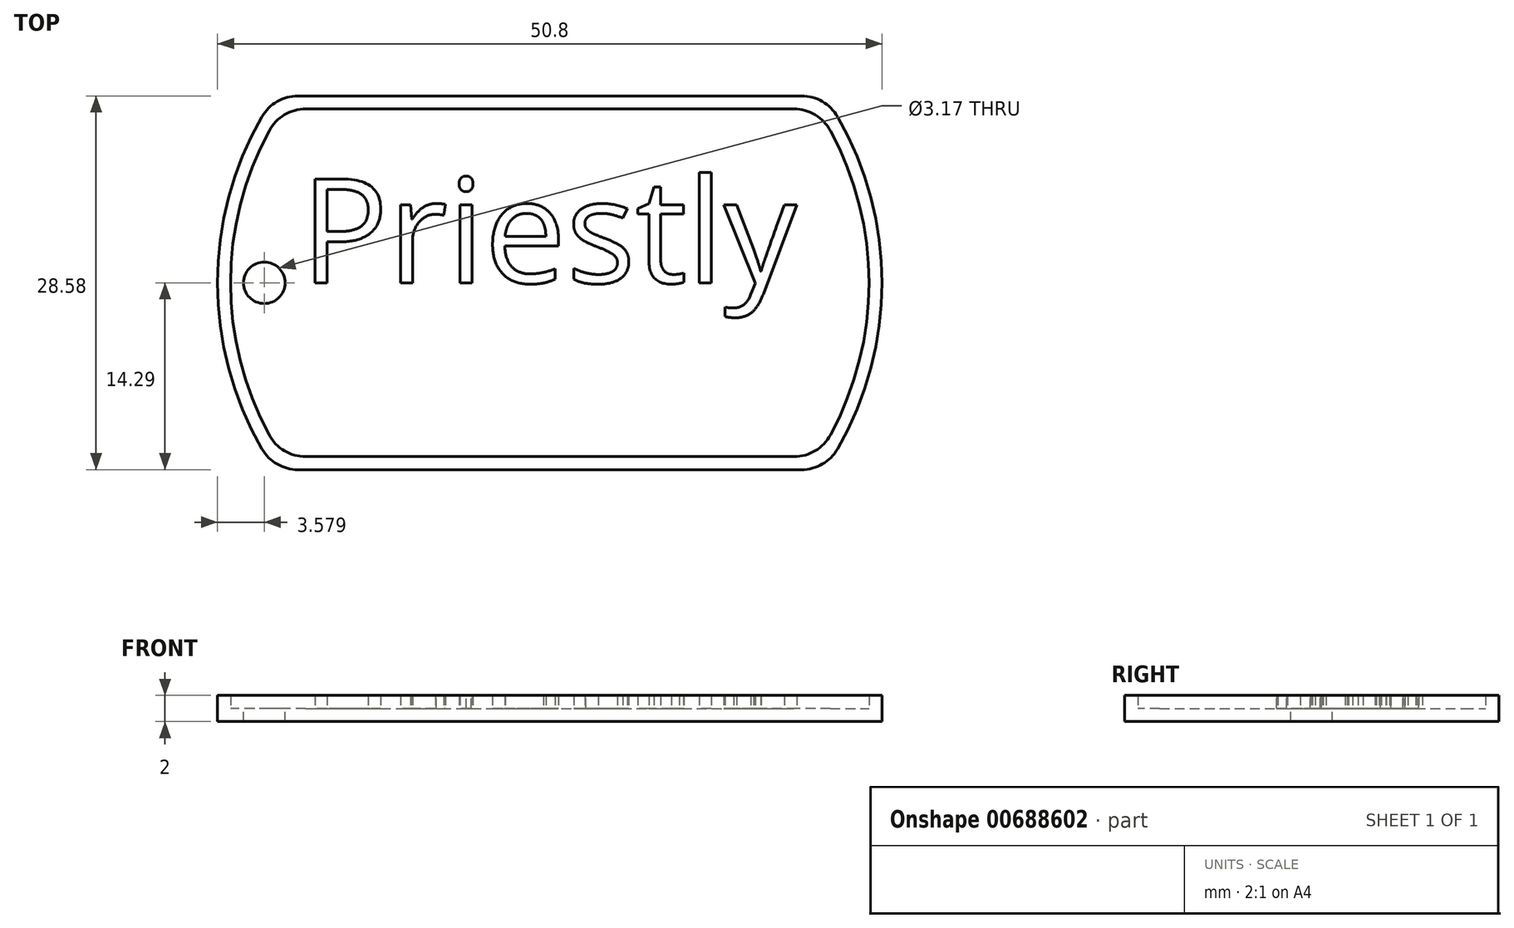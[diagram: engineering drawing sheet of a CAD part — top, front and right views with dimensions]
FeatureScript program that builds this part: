
annotation { "Feature Type Name" : "Feature", "Feature Type Description" : "" }
export const myFeature = defineFeature(function(context is Context, id is Id, definition is map)
    precondition{}
    {
        {
            var Q0;
            Q0=qCreatedBy(makeId("Top.planeOp"),FACE);
            var sketch = newSketch(context, id + "F0", { "sketchPlane" : qUnion([Q0])});
            skArc(sketch, "E0", {"start": v(-22, 12.7) * mm, "mid": v(-25.4, 0) * mm, "end": v(-22, -12.7) * mm});
            skLineSegment(sketch, "E1.top", {"start": v(-19.25, -14.29) * mm, "end": v(19.25, -14.29) * mm});
            skArc(sketch, "E2.trimOffspring", {"start": v(22, -12.7) * mm, "mid": v(25.4, 0) * mm, "end": v(22, 12.7) * mm});
            skLineSegment(sketch, "E3", {"start": v(-19.25, 14.29) * mm, "end": v(19.25, 14.29) * mm});
            skPoint(sketch, "E4.visualSharp", {"position": v(-21, 14.29) * mm});
            skArc(sketch, "E4.filletArc", {"start": v(-19.25, 14.29) * mm, "mid": v(-20.83, 13.86) * mm, "end": v(-22, 12.7) * mm});
            skPoint(sketch, "E5.visualSharp", {"position": v(21, 14.29) * mm});
            skArc(sketch, "E5.filletArc", {"start": v(22, 12.7) * mm, "mid": v(20.83, 13.86) * mm, "end": v(19.25, 14.29) * mm});
            skPoint(sketch, "E6.visualSharp", {"position": v(21, -14.29) * mm});
            skArc(sketch, "E6.filletArc", {"start": v(19.25, -14.29) * mm, "mid": v(20.83, -13.86) * mm, "end": v(22, -12.7) * mm});
            skPoint(sketch, "E7.visualSharp", {"position": v(-21, -14.29) * mm});
            skArc(sketch, "E7.filletArc", {"start": v(-22, -12.7) * mm, "mid": v(-20.83, -13.86) * mm, "end": v(-19.25, -14.29) * mm});
            skSolve(sketch);
        }
        {
            var Q0;
            Q0=makeQuery(id+"F0.imprint","IMPRINT",FACE,{"disambiguationData":[TD([[makeQuery(id+"F0.imprint","IMPRINT",EDGE,{"derivedFrom":sQuery(id+"F0.wireOp",EDGE,"E0")}),1.0]])]});
            extrude(context, id + "F1", {"entities" : qUnion([Q0]), "depth" : 1 * mm, "offsetDistance" : 25.4 * mm});
        }
        {
            var Q0;
            Q0=makeQuery(id+"F1.opExtrude","CAP_FACE",FACE,{"disambiguationData":[OSD([sQuery(id+"F0.wireOp",EDGE,"E0"),sQuery(id+"F0.wireOp",EDGE,"E1.top"),sQuery(id+"F0.wireOp",EDGE,"E2.trimOffspring"),sQuery(id+"F0.wireOp",EDGE,"E3"),sQuery(id+"F0.wireOp",EDGE,"E4.filletArc"),sQuery(id+"F0.wireOp",EDGE,"E5.filletArc"),sQuery(id+"F0.wireOp",EDGE,"E6.filletArc"),sQuery(id+"F0.wireOp",EDGE,"E7.filletArc")])],"isStart":false});
            var sketch = newSketch(context, id + "F2", { "sketchPlane" : qUnion([Q0])});
            skLineSegment(sketch, "E8.0", {"start": v(-18.66, 13.29) * mm, "end": v(18.66, 13.29) * mm});
            skArc(sketch, "E8.1", {"start": v(-21.45, 11.63) * mm, "mid": v(-24.4, 0) * mm, "end": v(-21.45, -11.63) * mm});
            skLineSegment(sketch, "E8.2", {"start": v(-18.66, -13.29) * mm, "end": v(18.66, -13.29) * mm});
            skArc(sketch, "E8.3", {"start": v(21.45, -11.63) * mm, "mid": v(24.4, 0) * mm, "end": v(21.45, 11.63) * mm});
            skPoint(sketch, "E9.visualSharp", {"position": v(-20.46, 13.29) * mm});
            skArc(sketch, "E9.filletArc", {"start": v(-18.66, 13.29) * mm, "mid": v(-20.29, 12.84) * mm, "end": v(-21.45, 11.63) * mm});
            skPoint(sketch, "E10.visualSharp", {"position": v(20.46, 13.29) * mm});
            skArc(sketch, "E10.filletArc", {"start": v(21.45, 11.63) * mm, "mid": v(20.29, 12.84) * mm, "end": v(18.66, 13.29) * mm});
            skPoint(sketch, "E11.visualSharp", {"position": v(20.46, -13.29) * mm});
            skArc(sketch, "E11.filletArc", {"start": v(18.66, -13.29) * mm, "mid": v(20.29, -12.84) * mm, "end": v(21.45, -11.63) * mm});
            skPoint(sketch, "E12.visualSharp", {"position": v(-20.46, -13.29) * mm});
            skArc(sketch, "E12.filletArc", {"start": v(-21.45, -11.63) * mm, "mid": v(-20.29, -12.84) * mm, "end": v(-18.66, -13.29) * mm});
            skLineSegment(sketch, "E13.0", {"start": v(-19.25, 14.29) * mm, "end": v(19.25, 14.29) * mm});
            skArc(sketch, "E13.1", {"start": v(-22, 12.7) * mm, "mid": v(-25.4, 0) * mm, "end": v(-22, -12.7) * mm});
            skLineSegment(sketch, "E13.2", {"start": v(-19.25, -14.29) * mm, "end": v(19.25, -14.29) * mm});
            skArc(sketch, "E13.3", {"start": v(22, -12.7) * mm, "mid": v(25.4, 0) * mm, "end": v(22, 12.7) * mm});
            skPoint(sketch, "E14.visualSharp", {"position": v(-21, -14.29) * mm});
            skArc(sketch, "E14.filletArc", {"start": v(-22, -12.7) * mm, "mid": v(-20.83, -13.86) * mm, "end": v(-19.25, -14.29) * mm});
            skPoint(sketch, "E15.visualSharp", {"position": v(21, -14.29) * mm});
            skArc(sketch, "E15.filletArc", {"start": v(19.25, -14.29) * mm, "mid": v(20.83, -13.86) * mm, "end": v(22, -12.7) * mm});
            skPoint(sketch, "E16.visualSharp", {"position": v(21, 14.29) * mm});
            skArc(sketch, "E16.filletArc", {"start": v(22, 12.7) * mm, "mid": v(20.83, 13.86) * mm, "end": v(19.25, 14.29) * mm});
            skPoint(sketch, "E17.visualSharp", {"position": v(-21, 14.29) * mm});
            skArc(sketch, "E17.filletArc", {"start": v(-19.25, 14.29) * mm, "mid": v(-20.83, 13.86) * mm, "end": v(-22, 12.7) * mm});
            skSolve(sketch);
        }
        {
            var Q0;
            Q0=makeQuery(id+"F2.imprint","IMPRINT",FACE,{"disambiguationData":[TD([[makeQuery(id+"F2.imprint","IMPRINT",EDGE,{"derivedFrom":sQuery(id+"F2.wireOp",EDGE,"E8.0")}),1.0]])]});
            extrude(context, id + "F3", {"entities" : qUnion([Q0]), "operationType" : NewBodyOperationType.ADD, "depth" : 1 * mm, "offsetDistance" : 25.4 * mm});
        }
        {
            var Q0;
            Q0=makeQuery(id+"F1.opExtrude","CAP_FACE",FACE,{"disambiguationData":[OSD([sQuery(id+"F0.wireOp",EDGE,"E0"),sQuery(id+"F0.wireOp",EDGE,"E1.top"),sQuery(id+"F0.wireOp",EDGE,"E2.trimOffspring"),sQuery(id+"F0.wireOp",EDGE,"E3"),sQuery(id+"F0.wireOp",EDGE,"E4.filletArc"),sQuery(id+"F0.wireOp",EDGE,"E5.filletArc"),sQuery(id+"F0.wireOp",EDGE,"E6.filletArc"),sQuery(id+"F0.wireOp",EDGE,"E7.filletArc")])],"isStart":false});
            var sketch = newSketch(context, id + "F4", { "sketchPlane" : qUnion([Q0])});
            skCircle(sketch, "E18", {"center": v(-21.82, 0) * mm, "radius": 1.59 * mm});
            skSolve(sketch);
        }
        {
            var Q0;
            Q0=makeQuery(id+"F4.imprint","IMPRINT",FACE,{"disambiguationData":[TD([[makeQuery(id+"F4.imprint","IMPRINT",EDGE,{"derivedFrom":sQuery(id+"F4.wireOp",EDGE,"E18")}),1.0]])]});
            extrude(context, id + "F5", {"entities" : qUnion([Q0]), "operationType" : NewBodyOperationType.REMOVE, "oppositeDirection" : true, "depth" : 1 * mm, "offsetDistance" : 25.4 * mm});
        }
        {
            var Q0;
            Q0=makeQuery(id+"F1.opExtrude","CAP_FACE",FACE,{"disambiguationData":[OSD([sQuery(id+"F0.wireOp",EDGE,"E0"),sQuery(id+"F0.wireOp",EDGE,"E1.top"),sQuery(id+"F0.wireOp",EDGE,"E2.trimOffspring"),sQuery(id+"F0.wireOp",EDGE,"E3"),sQuery(id+"F0.wireOp",EDGE,"E4.filletArc"),sQuery(id+"F0.wireOp",EDGE,"E5.filletArc"),sQuery(id+"F0.wireOp",EDGE,"E6.filletArc"),sQuery(id+"F0.wireOp",EDGE,"E7.filletArc")])],"isStart":false});
            var sketch = newSketch(context, id + "F6", { "sketchPlane" : qUnion([Q0])});
            skText(sketch, "E19", { "text": "Priestly", "fontName": "OpenSans-Regular.ttf"});
            const initialGuessF6  = {"E19": [-0.01905, 0, 1, 0, 0.00801]};
            skSetInitialGuess(sketch, initialGuessF6);
            skSolve(sketch);
        }
        {
            var Q0;
            Q0 = qSketchRegion(id + "F6", true);
            extrude(context, id + "F7", {"entities" : qUnion([Q0]), "operationType" : NewBodyOperationType.ADD, "depth" : 1 * mm, "offsetDistance" : 25.4 * mm});
        }
    });
